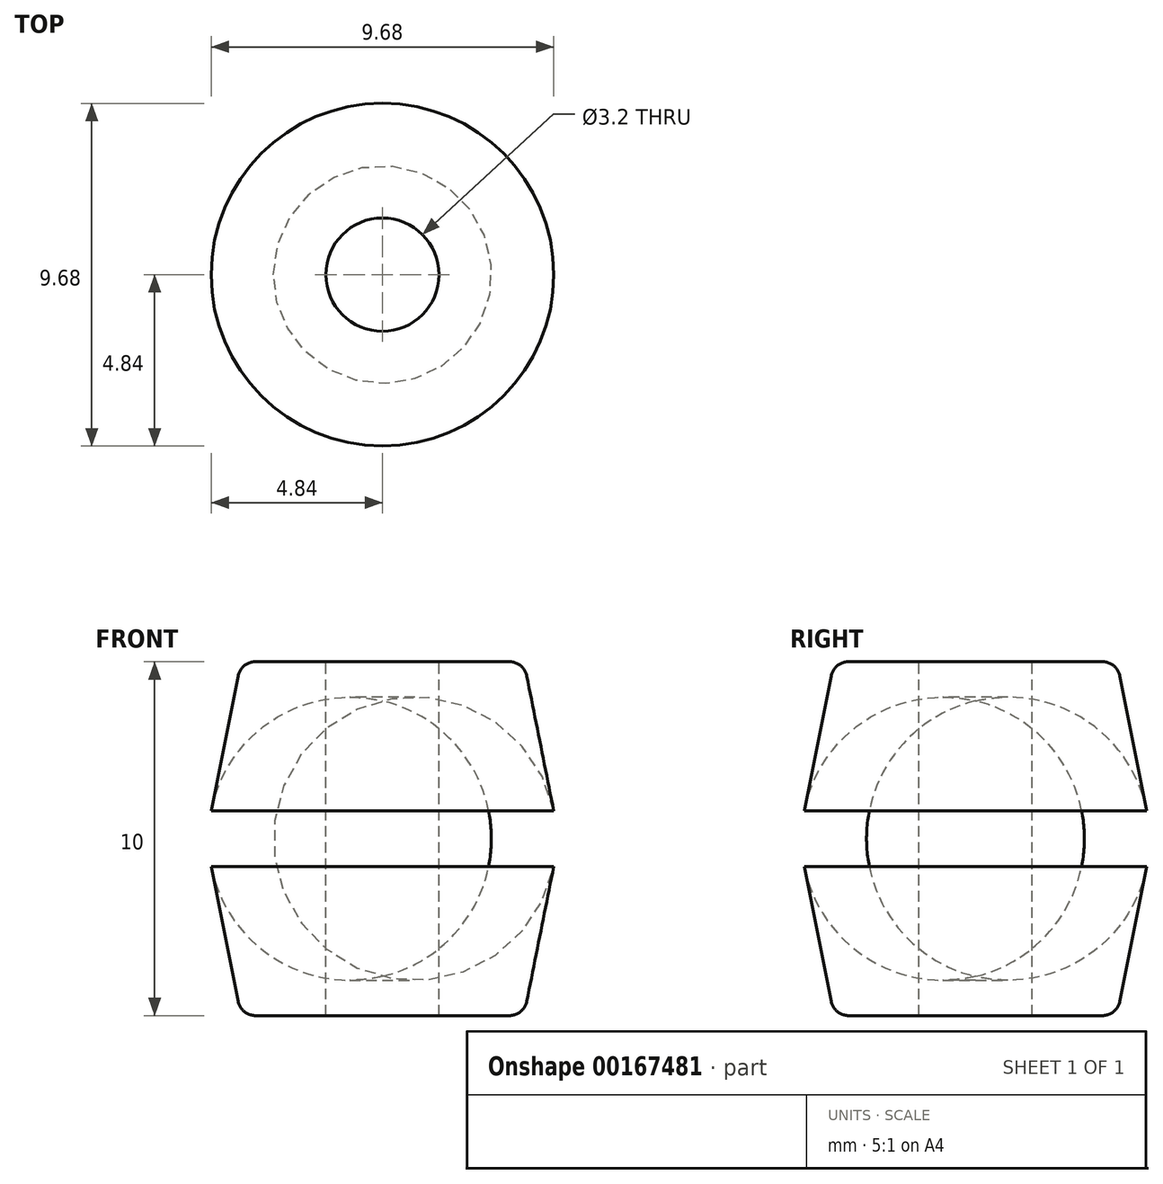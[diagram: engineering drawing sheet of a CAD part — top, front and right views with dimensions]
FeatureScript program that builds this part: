
annotation { "Feature Type Name" : "Feature", "Feature Type Description" : "" }
export const myFeature = defineFeature(function(context is Context, id is Id, definition is map)
    precondition{}
    {
        {
            var Q0;
            Q0=qCreatedBy(makeId("Front.planeOp"),FACE);
            var sketch = newSketch(context, id + "F0", { "sketchPlane" : qUnion([Q0])});
            skLineSegment(sketch, "E0", {"start": v(0, 0) * mm, "end": v(0, 5) * mm, "construction": true});
            skLineSegment(sketch, "E1", {"start": v(4.08, 4.6) * mm, "end": v(4.84, 0.78) * mm});
            skLineSegment(sketch, "E2", {"start": v(0, 5) * mm, "end": v(3.6, 5) * mm});
            skLineSegment(sketch, "E3.MirrorCS", {"start": v(0, -5) * mm, "end": v(3.6, -5) * mm});
            skLineSegment(sketch, "E4.MirrorCS", {"start": v(4.08, -4.6) * mm, "end": v(4.84, -0.78) * mm});
            skPoint(sketch, "E5.visualSharp", {"position": v(4, 5) * mm});
            skArc(sketch, "E5.filletArc", {"start": v(4.08, 4.6) * mm, "mid": v(3.9, 4.89) * mm, "end": v(3.6, 5) * mm});
            skPoint(sketch, "E6.visualSharp", {"position": v(4, -5) * mm});
            skArc(sketch, "E6.filletArc", {"start": v(3.6, -5) * mm, "mid": v(3.9, -4.89) * mm, "end": v(4.08, -4.6) * mm});
            skPoint(sketch, "E7.visualSharp", {"position": v(5, 0) * mm});
            skArc(sketch, "E7.filletArc", {"start": v(4.84, -0.78) * mm, "mid": v(4.92, 0) * mm, "end": v(4.84, 0.78) * mm});
            skLineSegment(sketch, "E8", {"start": v(0, 5) * mm, "end": v(0, -5) * mm});
            skSolve(sketch);
        }
        {
            var Q0;
            Q0=makeQuery(id+"F0.imprint","IMPRINT",FACE,{"disambiguationData":[TD([[makeQuery(id+"F0.imprint","IMPRINT",EDGE,{"derivedFrom":sQuery(id+"F0.wireOp",EDGE,"E1")}),-1.0]])]});
            var Q1;
            Q1=sQuery(id+"F0.wireOp",EDGE,"E8");
            revolve(context, id + "F1", {"entities" : qUnion([Q0]), "axis" : qUnion([Q1]), "revolveType" : RevolveType.FULL});
        }
        {
            var Q0;
            Q0=makeQuery(id+"F1.opRevolve","SWEPT_FACE",FACE,{"disambiguationData":[OSD([sQuery(id+"F0.wireOp",EDGE,"E2")])]});
            var sketch = newSketch(context, id + "F2", { "sketchPlane" : qUnion([Q0])});
            skCircle(sketch, "E9", {"center": v(0, 0) * mm, "radius": 1.6 * mm});
            skSolve(sketch);
        }
        {
            var Q0;
            Q0=makeQuery(id+"F2.imprint","IMPRINT",FACE,{"disambiguationData":[TD([[makeQuery(id+"F2.imprint","IMPRINT",EDGE,{"derivedFrom":sQuery(id+"F2.wireOp",EDGE,"E9")}),1.0]])]});
            extrude(context, id + "F3", {"entities" : qUnion([Q0]), "operationType" : NewBodyOperationType.REMOVE, "endBound" : BoundingType.THROUGH_ALL, "oppositeDirection" : true, "depth" : 25 * mm});
        }
    });
